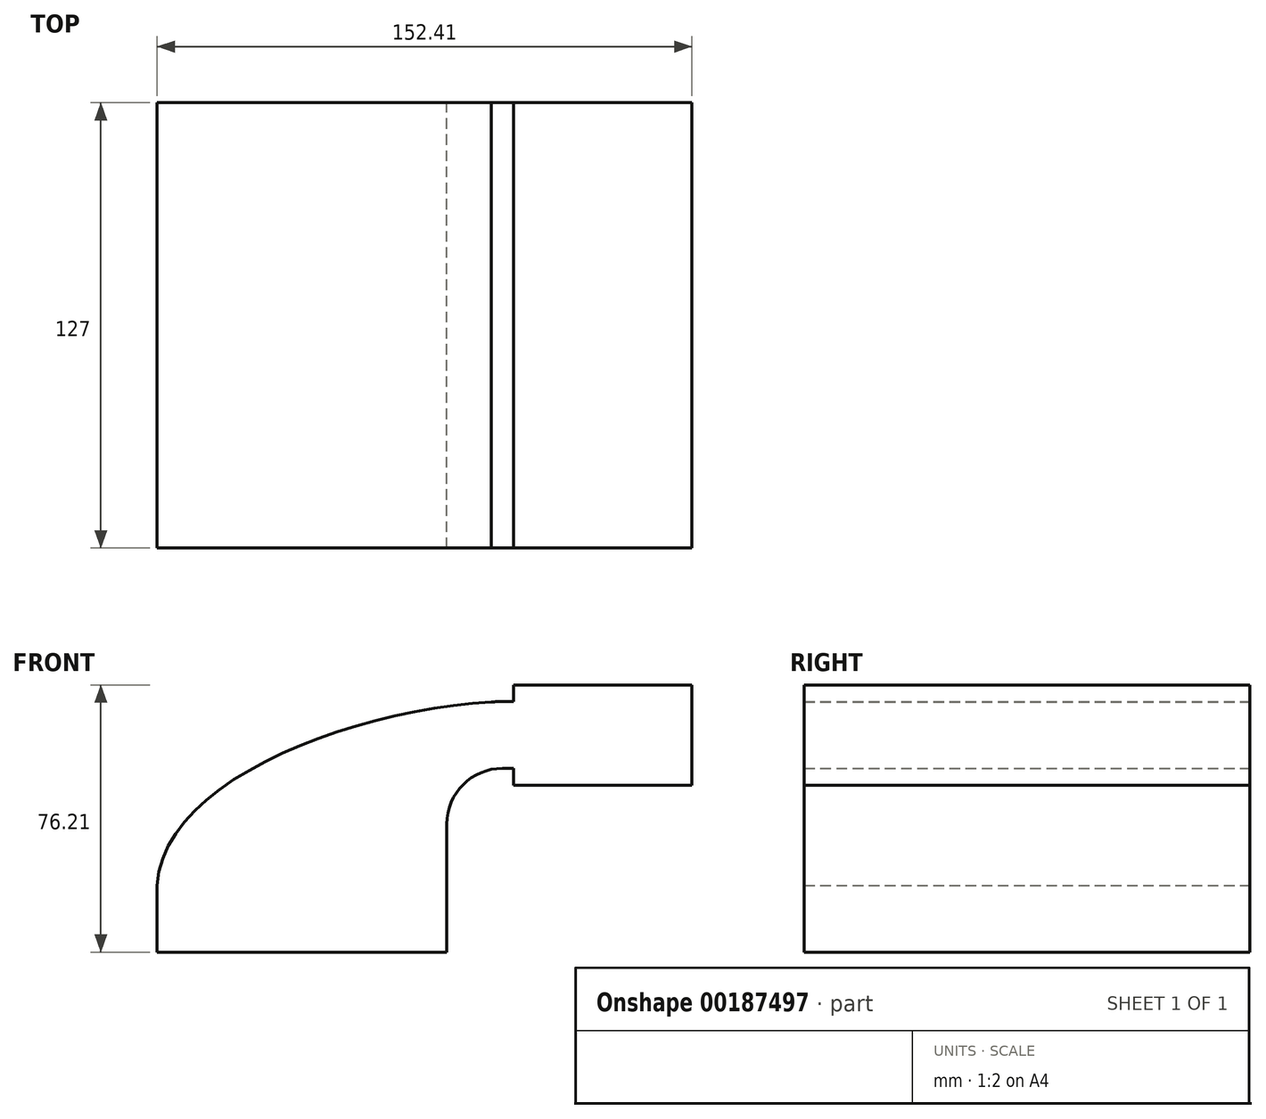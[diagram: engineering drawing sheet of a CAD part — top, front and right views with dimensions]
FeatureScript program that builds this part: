
annotation { "Feature Type Name" : "Feature", "Feature Type Description" : "" }
export const myFeature = defineFeature(function(context is Context, id is Id, definition is map)
    precondition{}
    {
        {
            var Q0;
            Q0=qCreatedBy(makeId("Front.planeOp"),FACE);
            var sketch = newSketch(context, id + "F0", { "sketchPlane" : qUnion([Q0])});
            skLineSegment(sketch, "E0.rect.bottom", {"start": v(-41.28, 9.52) * mm, "end": v(41.28, 9.52) * mm});
            skLineSegment(sketch, "E0.rect.top", {"start": v(-41.28, -9.52) * mm, "end": v(41.28, -9.52) * mm});
            skLineSegment(sketch, "E0.rect.left", {"start": v(-41.28, 9.52) * mm, "end": v(-41.28, -9.52) * mm});
            skLineSegment(sketch, "E0.rect.right", {"start": v(41.28, 9.52) * mm, "end": v(41.28, -9.52) * mm});
            skPoint(sketch, "E0.rect.middle", {"position": v(0, 0) * mm});
            skLineSegment(sketch, "E1", {"start": v(41.28, 9.52) * mm, "end": v(41.28, 27) * mm});
            skArc(sketch, "E2", {"start": v(41.28, 27) * mm, "mid": v(45.92, 38.23) * mm, "end": v(57.15, 42.88) * mm});
            skLineSegment(sketch, "E3", {"start": v(57.15, 42.88) * mm, "end": v(85.72, 42.88) * mm});
            skLineSegment(sketch, "E4.rect.bottom", {"start": v(60.32, 38.1) * mm, "end": v(111.12, 38.1) * mm});
            skLineSegment(sketch, "E4.rect.top", {"start": v(60.32, 66.68) * mm, "end": v(111.12, 66.68) * mm});
            skLineSegment(sketch, "E4.rect.left", {"start": v(60.32, 38.1) * mm, "end": v(60.32, 66.68) * mm});
            skLineSegment(sketch, "E4.rect.right", {"start": v(111.13, 38.1) * mm, "end": v(111.12, 66.68) * mm});
            skPoint(sketch, "E4.rect.middle", {"position": v(85.72, 52.39) * mm});
            skLineSegment(sketch, "E5.0", {"start": v(57.15, 61.93) * mm, "end": v(85.72, 61.93) * mm});
            skArc(sketch, "E5.1", {"start": v(22.23, 27) * mm, "mid": v(32.45, 51.7) * mm, "end": v(57.15, 61.93) * mm});
            skLineSegment(sketch, "E5.2", {"start": v(22.23, 9.52) * mm, "end": v(22.23, 27) * mm});
            skLineSegment(sketch, "E6", {"start": v(85.72, 38.1) * mm, "end": v(85.72, 66.68) * mm});
            skFitSpline(sketch, "E7", {"points": [v(-41.28, 9.53) * mm, v(57.15, 61.93) * mm], "startDerivative": vector(5.2, 92.34) * mm, "endDerivative": vector(120.92, 4.22) * mm});
            skSolve(sketch);
        }
        {
            var Q0;
            Q0 = qSketchRegion(id + "F0", true);
            extrude(context, id + "F1", {"entities" : qUnion([Q0]), "endBound" : BoundingType.SYMMETRIC, "depth" : 127 * mm});
        }
    });
